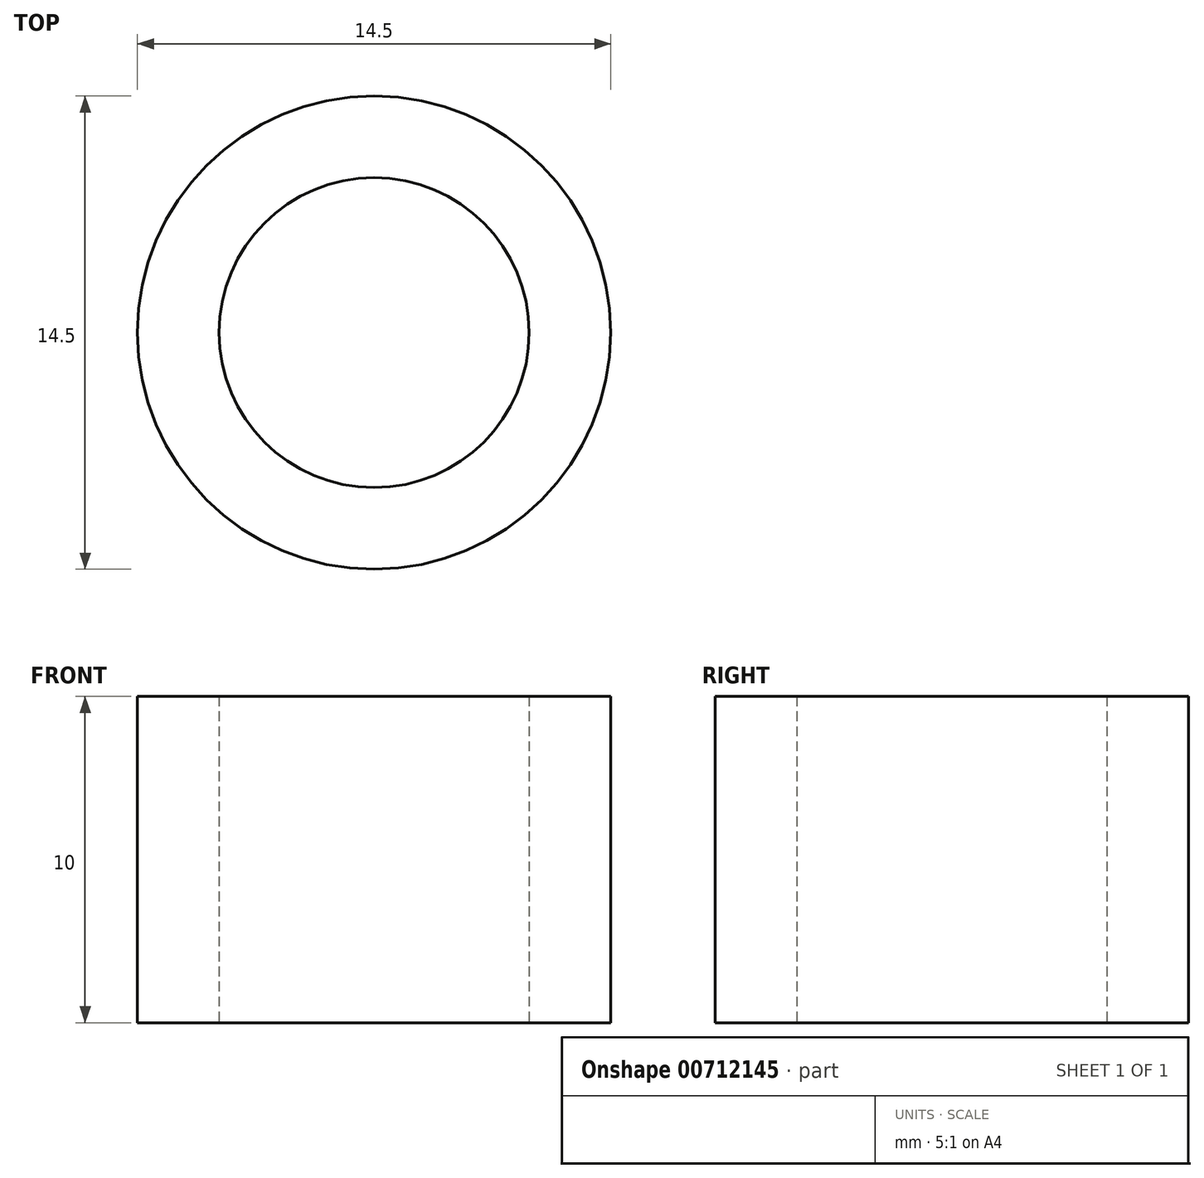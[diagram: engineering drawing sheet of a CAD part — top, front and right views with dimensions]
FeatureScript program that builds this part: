
annotation { "Feature Type Name" : "Feature", "Feature Type Description" : "" }
export const myFeature = defineFeature(function(context is Context, id is Id, definition is map)
    precondition{}
    {
        {
            var Q0;
            Q0=qCreatedBy(makeId("Top.planeOp"),FACE);
            var sketch = newSketch(context, id + "F0", { "sketchPlane" : qUnion([Q0])});
            skCircle(sketch, "E0", {"center": v(0, 0) * mm, "radius": 4.75 * mm});
            skCircle(sketch, "E1", {"center": v(0, 0) * mm, "radius": 7.25 * mm});
            skSolve(sketch);
        }
        {
            var Q0;
            Q0=makeQuery(id+"F0.imprint","IMPRINT",FACE,{"disambiguationData":[TD([[makeQuery(id+"F0.imprint","IMPRINT",EDGE,{"derivedFrom":sQuery(id+"F0.wireOp",EDGE,"E0")}),-1.0]])]});
            extrude(context, id + "F1", {"entities" : qUnion([Q0]), "depth" : 10 * mm, "offsetDistance" : 25 * mm});
        }
    });
